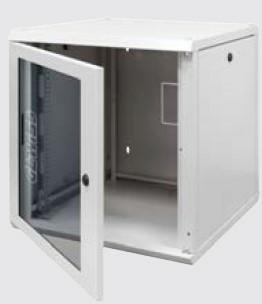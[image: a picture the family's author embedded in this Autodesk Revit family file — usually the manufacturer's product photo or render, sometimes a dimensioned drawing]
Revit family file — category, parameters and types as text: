
# Revit family: Domotics-CablaggioStrutturato-GEWISS-QUADRI_PARETE_19_9U_P400
name_source: partatom
category: Apparecchi elettrici
units: mm (PartAtom-declared; Revit-internal decimal feet)

## family parameters
Condiviso = No
Host = Superficie
Mantenere orientamento annotazione = Sì
Punto di calcolo locali = Sì
Quota connettore circolare = Usa diametro
Taglio con vuoti quando caricato = No
Tipo di parte = Normale

## types (1)
- Domotics-CablaggioStrutturato-GEWISS-QUADRI_PARETE_19_9U_P400
    Apertura porta = 180°
    Catalogo = DOMOTICS
    Categoria = Quadro da parete 19"
    Codice Electrocod = 3752
    Colore = Grigio (RAL 7035)
    Descrizione = QUADRO DA PARETE 19 9U P=400MM.
    Dim. esterne BxHxP (mm) = 600x470x400
    Finitura = Bucciata
    Grado di protezione = IP20
    IDF = 30d53955-7ab3-4fb3-a222-ebd7328e8131
    IDT = ea368ef7b3c0440fbd5b55759d12ab1b
    Immagine tipo = B.jpg
    Materiale = Acciaio
    Modello = GW38407
    N. montanti = 2
    Portata statica = 50KG
    Produttore = GEWISS S.p.A.
    Profondità (mm) = 400 mm
    Prospetto di default = 1219 mm
    SEO = Quadro
    Scheda Tecnica = https://www.gewiss.com
    Tipologia porta = Reversibile
    URL = https://www.gewiss.com
    Unità di cablaggio = 9 U
    Versione file RFA = 21.2

## geometry (parser evidence)
native form markers: Sweep x3
no freeform markers — native parametric forms only
